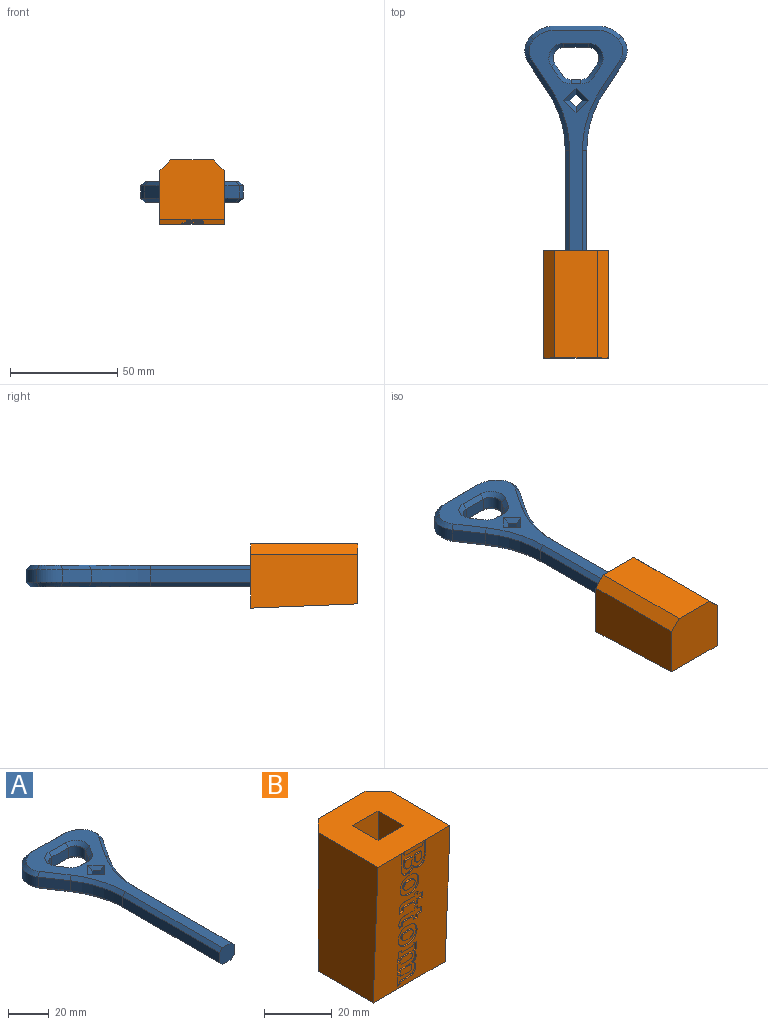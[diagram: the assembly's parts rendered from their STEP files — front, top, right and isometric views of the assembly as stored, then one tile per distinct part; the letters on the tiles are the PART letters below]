
ASSEMBLY  parts=2 mates=1
PART A: 72 faces, bbox 47.8x125x10 mm
  f0: plane 123x43.75mm, normal (0,0,1), area 1271.6mm2, adj f4,f33,f34,f35,f36,f37,f38,f39
  f1: plane 123x43.75mm, normal (0,0,-1), area 1271.6mm2, adj f4,f22,f23,f24,f25,f26,f27,f28
  f2: plane 13.2x8.8mm, normal (-0.83,-0.55,0), area 95.2mm2, adj f19,f20,f24,f35
  f3: plane 66.83x6mm, normal (-1,0,0), area 401mm2, adj f4,f20,f22,f33
  f4: plane 10x10mm, normal (0,-1,0), area 92mm2, adj f0,f1,f3,f5,f22,f32,f33,f43
  f5: plane 66.83x6mm, normal (1,0,0), area 401mm2, adj f4,f21,f32,f43
  f6: plane 13.2x8.8mm, normal (0.83,-0.55,0), area 95.2mm2, adj f18,f21,f30,f41
  f7: plane 20.26x6mm, normal (0,1,0), area 121.6mm2, adj f16,f17,f27,f38
  f8: plane 11.32x6mm, normal (0,-1,0), area 67.9mm2, adj f12,f15,f51,f52
  f9: plane 6x5mm, normal (-0.83,0.55,0), area 36.1mm2, adj f12,f13,f48,f56
  f10: plane 6x4.65mm, normal (0,1,0), area 27.9mm2, adj f13,f14,f44,f59
  f11: plane 6x5mm, normal (0.83,0.55,0), area 36.1mm2, adj f14,f15,f47,f55
  f12: cylinder r=5mm len=7.77mm, axis (0,0,-1), area 64.8mm2, adj f8,f9,f50,f54
  f13: cylinder r=5mm len=6mm, axis (0,0,1), area 29.5mm2, adj f9,f10,f46,f58
  f14: cylinder r=5mm len=6mm, axis (0,0,1), area 29.5mm2, adj f10,f11,f45,f57
  f15: cylinder r=5mm len=7.77mm, axis (0,0,-1), area 64.8mm2, adj f8,f11,f49,f53
  f16: cylinder r=15mm len=11.24mm, axis (0,0,-1), area 76.2mm2, adj f7,f18,f28,f39
  f17: cylinder r=15mm len=11.24mm, axis (0,0,1), area 76.2mm2, adj f7,f19,f26,f37
  f18: cylinder r=10mm len=12.17mm, axis (0,0,-1), area 78.7mm2, adj f6,f16,f29,f40
  f19: cylinder r=10mm len=12.17mm, axis (0,0,1), area 78.7mm2, adj f2,f17,f25,f36
  f20: cylinder r=50mm len=27.74mm, axis (0,0,-1), area 176.4mm2, adj f2,f3,f23,f34
  f21: cylinder r=50mm len=27.74mm, axis (0,0,-1), area 176.4mm2, adj f5,f6,f31,f42
  f22: plane 66.83x2mm, normal (-0.71,0,-0.71), area 189mm2, adj f1,f3,f4,f23
  f23: cone r=52mm half-angle=45deg, axis (0,0,-1), area 84.8mm2, adj f1,f20,f22,f24
  f24: plane 14.31x10.46mm, normal (-0.59,-0.39,-0.71), area 44.9mm2, adj f1,f2,f23,f25
  f25: cone r=8mm half-angle=45deg, axis (0,0,1), area 33.4mm2, adj f1,f19,f24,f26
  f26: cone r=13mm half-angle=45deg, axis (0,0,1), area 33.5mm2, adj f1,f17,f25,f27
  f27: plane 20.26x2mm, normal (0,0.71,-0.71), area 57.3mm2, adj f1,f7,f26,f28
  f28: cone r=13mm half-angle=45deg, axis (0,0,1), area 33.5mm2, adj f1,f16,f27,f29
  f29: cone r=8mm half-angle=45deg, axis (0,0,1), area 33.4mm2, adj f1,f18,f28,f30
  f30: plane 14.31x10.46mm, normal (0.59,-0.39,-0.71), area 44.9mm2, adj f1,f6,f29,f31
  f31: cone r=52mm half-angle=45deg, axis (0,0,-1), area 84.8mm2, adj f1,f21,f30,f32
  f32: plane 66.83x2mm, normal (0.71,0,-0.71), area 189mm2, adj f1,f4,f5,f31
  f33: plane 66.83x2mm, normal (-0.71,0,0.71), area 189mm2, adj f0,f3,f4,f34
  f34: cone r=52mm half-angle=45deg, axis (0,0,1), area 84.8mm2, adj f0,f20,f33,f35
  f35: plane 14.31x10.46mm, normal (-0.59,-0.39,0.71), area 44.9mm2, adj f0,f2,f34,f36
  f36: cone r=8mm half-angle=45deg, axis (0,0,-1), area 33.4mm2, adj f0,f19,f35,f37
  f37: cone r=13mm half-angle=45deg, axis (0,0,-1), area 33.5mm2, adj f0,f17,f36,f38
  f38: plane 20.26x2mm, normal (0,0.71,0.71), area 57.3mm2, adj f0,f7,f37,f39
  f39: cone r=13mm half-angle=45deg, axis (0,0,-1), area 33.5mm2, adj f0,f16,f38,f40
  f40: cone r=8mm half-angle=45deg, axis (0,0,-1), area 33.4mm2, adj f0,f18,f39,f41
  f41: plane 14.31x10.46mm, normal (0.59,-0.39,0.71), area 44.9mm2, adj f0,f6,f40,f42
  f42: cone r=52mm half-angle=45deg, axis (0,0,1), area 84.8mm2, adj f0,f21,f41,f43
  f43: plane 66.83x2mm, normal (0.71,0,0.71), area 189mm2, adj f0,f4,f5,f42
  f44: plane 4.65x2mm, normal (0,0.71,-0.71), area 13.1mm2, adj f1,f10,f45,f46
  f45: cone r=7mm half-angle=45deg, axis (0,0,-1), area 16.7mm2, adj f1,f14,f44,f47
  f46: cone r=7mm half-angle=45deg, axis (0,0,-1), area 16.7mm2, adj f1,f13,f44,f48
  f47: plane 6.11x5mm, normal (0.59,0.39,-0.71), area 17mm2, adj f1,f11,f45,f49
  f48: plane 6.11x5mm, normal (-0.59,0.39,-0.71), area 17mm2, adj f1,f9,f46,f50
  f49: cone r=7mm half-angle=45deg, axis (0,0,-1), area 36.6mm2, adj f1,f15,f47,f51
  f50: cone r=7mm half-angle=45deg, axis (0,0,-1), area 36.6mm2, adj f1,f12,f48,f51
  f51: plane 11.32x2mm, normal (0,-0.71,-0.71), area 32mm2, adj f1,f8,f49,f50
  f52: plane 11.32x2mm, normal (0,-0.71,0.71), area 32mm2, adj f0,f8,f53,f54
  f53: cone r=7mm half-angle=45deg, axis (0,0,1), area 36.6mm2, adj f0,f15,f52,f55
  f54: cone r=7mm half-angle=45deg, axis (0,0,1), area 36.6mm2, adj f0,f12,f52,f56
  f55: plane 6.11x5mm, normal (0.59,0.39,0.71), area 17mm2, adj f0,f11,f53,f57
  f56: plane 6.11x5mm, normal (-0.59,0.39,0.71), area 17mm2, adj f0,f9,f54,f58
  f57: cone r=7mm half-angle=45deg, axis (0,0,1), area 16.7mm2, adj f0,f14,f55,f59
  f58: cone r=7mm half-angle=45deg, axis (0,0,1), area 16.7mm2, adj f0,f13,f56,f59
  f59: plane 4.65x2mm, normal (0,0.71,0.71), area 13.1mm2, adj f0,f10,f57,f58
  f60: plane 6x2.83mm, normal (0.71,0.71,0), area 24mm2, adj f61,f63,f67,f71
  f61: plane 6x2.83mm, normal (-0.71,0.71,0), area 24mm2, adj f60,f62,f65,f69
  f62: plane 6x2.83mm, normal (-0.71,-0.71,0), area 24mm2, adj f61,f63,f64,f68
  f63: plane 6x2.83mm, normal (0.71,-0.71,0), area 24mm2, adj f60,f62,f66,f70
  f64: plane 5.66x5.66mm, normal (-0.5,-0.5,-0.71), area 17mm2, adj f1,f62,f65,f66
  f65: plane 5.66x5.66mm, normal (-0.5,0.5,-0.71), area 17mm2, adj f1,f61,f64,f67
  f66: plane 5.66x5.66mm, normal (0.5,-0.5,-0.71), area 17mm2, adj f1,f63,f64,f67
  f67: plane 5.66x5.66mm, normal (0.5,0.5,-0.71), area 17mm2, adj f1,f60,f65,f66
  f68: plane 5.66x5.66mm, normal (-0.5,-0.5,0.71), area 17mm2, adj f0,f62,f69,f70
  f69: plane 5.66x5.66mm, normal (-0.5,0.5,0.71), area 17mm2, adj f0,f61,f68,f71
  f70: plane 5.66x5.66mm, normal (0.5,-0.5,0.71), area 17mm2, adj f0,f63,f68,f71
  f71: plane 5.66x5.66mm, normal (0.5,0.5,0.71), area 17mm2, adj f0,f60,f69,f70
PART B: 175 faces, bbox 30x30x50 mm
  f0: plane 50x30mm, normal (0,-1,-0.04), area 1230.9mm2, adj f2,f7,f8,f10,f11,f12,f13,f14
  f1: plane 50x20mm, normal (0,1,0), area 1000mm2, adj f8,f10,f173,f174
  f2: plane 50x25mm, normal (-1,0,0), area 1200mm2, adj f0,f8,f10,f173
  f3: plane 20x10.5mm, normal (1,0,0), area 210mm2, adj f4,f6,f8,f9
  f4: plane 20x10.5mm, normal (0,-1,0), area 210mm2, adj f3,f5,f8,f9
  f5: plane 20x10.5mm, normal (-1,0,0), area 210mm2, adj f4,f6,f8,f9
  f6: plane 20x10.5mm, normal (0,1,0), area 210mm2, adj f3,f5,f8,f9
  f7: plane 50x25mm, normal (1,0,0), area 1200mm2, adj f0,f8,f10,f174
  f8: plane 30x30mm, normal (0,0,1), area 764.7mm2, adj f0,f1,f2,f3,f4,f5,f6,f7
  f9: plane 10.5x10.5mm, normal (0,0,1), area 110.3mm2, adj f3,f4,f5,f6
  f10: plane 30x28mm, normal (0,0,-1), area 815mm2, adj f0,f1,f2,f7,f173,f174
  f11: plane 2.04x0.58mm, normal (-1,0,0), area 1mm2, adj f0,f12,f30,f31
  f12: plane 1.84x0.5mm, normal (0,0.04,-1), area 0.9mm2, adj f0,f11,f13,f31
  f13: plane 1.12x0.54mm, normal (-1,0,0), area 0.6mm2, adj f0,f12,f14,f31
  f14: plane 1.42x0.5mm, normal (0,0.04,-1), area 0.7mm2, adj f0,f13,f15,f31
  f15: plane 1.12x0.54mm, normal (1,0,0), area 0.6mm2, adj f0,f14,f16,f31
  f16: plane 3.84x0.5mm, normal (0,0.04,-1), area 1.9mm2, adj f0,f15,f17,f31
  f17: extruded ~1.83x0.59mm, area 1mm2, adj f0,f16,f18,f31
  f18: extruded ~1.64x0.58mm, area 0.9mm2, adj f0,f17,f19,f31
  f19: extruded ~0.74x0.53mm, area 0.4mm2, adj f0,f18,f20,f31
  f20: extruded ~0.69x0.53mm, area 0.3mm2, adj f0,f19,f21,f31
  f21: plane 1.47x0.51mm, normal (-0.12,-0.04,0.99), area 0.7mm2, adj f0,f20,f22,f31
  f22: extruded ~0.51x0.37mm, area 0.2mm2, adj f0,f21,f23,f31
  f23: extruded ~0.51x0.38mm, area 0.2mm2, adj f0,f22,f24,f31
  f24: extruded ~0.52x0.51mm, area 0.3mm2, adj f0,f23,f25,f31
  f25: extruded ~0.63x0.51mm, area 0.3mm2, adj f0,f24,f26,f31
  f26: plane 3.83x0.5mm, normal (0,-0.04,1), area 1.9mm2, adj f0,f25,f27,f31
  f27: plane 1.34x0.55mm, normal (1,0,0), area 0.7mm2, adj f0,f26,f28,f31
  f28: plane 1.42x0.5mm, normal (0,-0.04,1), area 0.7mm2, adj f0,f27,f29,f31
  f29: plane 1.34x0.55mm, normal (-1,0,0), area 0.7mm2, adj f0,f28,f30,f31
  f30: plane 1.84x0.5mm, normal (0,-0.04,1), area 0.9mm2, adj f0,f11,f29,f31
  f31: plane 9.51x4.68mm, normal (0,-1,-0.04), area 24.2mm2, adj f11,f12,f13,f14,f15,f16,f17,f18
  f32: plane 0.5x0.15mm, normal (0,0.04,-1), area 0.1mm2, adj f0,f33,f51,f52
  f33: extruded ~2.76x0.96mm, area 1.5mm2, adj f0,f32,f34,f52
  f34: extruded ~2.63x1.07mm, area 1.5mm2, adj f0,f33,f35,f52
  f35: extruded ~2.61x1.07mm, area 1.4mm2, adj f0,f34,f36,f52
  f36: extruded ~2.76x0.96mm, area 1.5mm2, adj f0,f35,f37,f52
  f37: plane 0.5x0.15mm, normal (0,-0.04,1), area 0.1mm2, adj f0,f36,f38,f52
  f38: extruded ~2.76x0.96mm, area 1.5mm2, adj f0,f37,f39,f52
  f39: extruded ~2.63x1.07mm, area 1.5mm2, adj f0,f38,f40,f52
  f40: extruded ~2.62x1.07mm, area 1.5mm2, adj f0,f39,f51,f52
  f41: plane 0.5x0.15mm, normal (0,-0.04,1), area 0.1mm2, adj f42,f50,f52,f53
  f42: extruded ~1.63x0.51mm, area 0.8mm2, adj f41,f43,f52,f53
  f43: extruded ~1.17x0.63mm, area 0.7mm2, adj f42,f44,f52,f53
  f44: extruded ~1.18x0.63mm, area 0.7mm2, adj f43,f45,f52,f53
  f45: extruded ~1.63x0.51mm, area 0.8mm2, adj f44,f46,f52,f53
  f46: plane 0.5x0.15mm, normal (0,0.04,-1), area 0.1mm2, adj f45,f47,f52,f53
  f47: extruded ~1.65x0.51mm, area 0.9mm2, adj f46,f48,f52,f53
  f48: extruded ~1.17x0.63mm, area 0.7mm2, adj f47,f49,f52,f53
  f49: extruded ~1.19x0.62mm, area 0.7mm2, adj f48,f50,f52,f53
  f50: extruded ~1.65x0.51mm, area 0.9mm2, adj f41,f49,f52,f53
  f51: extruded ~2.76x0.96mm, area 1.5mm2, adj f0,f32,f40,f52
  f52: plane 7.8x7.09mm, normal (0,-1,-0.04), area 33.2mm2, adj f32,f33,f34,f35,f36,f37,f38,f39
  f53: plane 4.69x3.04mm, normal (0,-1,-0.04), area 11.9mm2, adj f41,f42,f43,f44,f45,f46,f47,f48
  f54: plane 0.5x0.15mm, normal (0,0.04,-1), area 0.1mm2, adj f0,f55,f73,f74
  f55: extruded ~2.76x0.96mm, area 1.5mm2, adj f0,f54,f56,f74
  f56: extruded ~2.63x1.07mm, area 1.5mm2, adj f0,f55,f57,f74
  f57: extruded ~2.61x1.07mm, area 1.4mm2, adj f0,f56,f58,f74
  f58: extruded ~2.76x0.96mm, area 1.5mm2, adj f0,f57,f59,f74
  f59: plane 0.5x0.15mm, normal (0,-0.04,1), area 0.1mm2, adj f0,f58,f60,f74
  f60: extruded ~2.76x0.96mm, area 1.5mm2, adj f0,f59,f61,f74
  f61: extruded ~2.63x1.07mm, area 1.5mm2, adj f0,f60,f62,f74
  f62: extruded ~2.62x1.07mm, area 1.5mm2, adj f0,f61,f73,f74
  f63: plane 0.5x0.15mm, normal (0,-0.04,1), area 0.1mm2, adj f64,f72,f74,f75
  f64: extruded ~1.63x0.51mm, area 0.8mm2, adj f63,f65,f74,f75
  f65: extruded ~1.17x0.63mm, area 0.7mm2, adj f64,f66,f74,f75
  f66: extruded ~1.18x0.63mm, area 0.7mm2, adj f65,f67,f74,f75
  f67: extruded ~1.63x0.51mm, area 0.8mm2, adj f66,f68,f74,f75
  f68: plane 0.5x0.15mm, normal (0,0.04,-1), area 0.1mm2, adj f67,f69,f74,f75
  f69: extruded ~1.65x0.51mm, area 0.9mm2, adj f68,f70,f74,f75
  f70: extruded ~1.17x0.63mm, area 0.7mm2, adj f69,f71,f74,f75
  f71: extruded ~1.19x0.62mm, area 0.7mm2, adj f70,f72,f74,f75
  f72: extruded ~1.65x0.51mm, area 0.9mm2, adj f63,f71,f74,f75
  f73: extruded ~2.76x0.96mm, area 1.5mm2, adj f0,f54,f62,f74
  f74: plane 7.8x7.09mm, normal (0,-1,-0.04), area 33.2mm2, adj f54,f55,f56,f57,f58,f59,f60,f61
  f75: plane 4.69x3.04mm, normal (0,-1,-0.04), area 11.9mm2, adj f63,f64,f65,f66,f67,f68,f69,f70
  f76: plane 1.1x0.54mm, normal (0.98,0.01,-0.19), area 0.6mm2, adj f0,f77,f118,f119
  f77: plane 4.66x0.5mm, normal (0,0.04,-1), area 2.3mm2, adj f0,f76,f78,f119
  f78: plane 1x0.54mm, normal (-0.98,0.01,-0.21), area 0.5mm2, adj f0,f77,f79,f119
  f79: plane 1.22x0.5mm, normal (0,0.04,-1), area 0.6mm2, adj f0,f78,f80,f119
  f80: plane 3.89x0.65mm, normal (1,0,0), area 1.9mm2, adj f0,f79,f81,f119
  f81: plane 1.22x0.5mm, normal (0,-0.04,1), area 0.6mm2, adj f0,f80,f82,f119
  f82: plane 0.89x0.53mm, normal (-0.97,-0.01,0.23), area 0.4mm2, adj f0,f81,f83,f119
  f83: plane 4.06x0.5mm, normal (0,-0.04,1), area 2mm2, adj f0,f82,f84,f119
  f84: extruded ~0.53x0.52mm, area 0.3mm2, adj f0,f83,f85,f119
  f85: extruded ~0.74x0.53mm, area 0.4mm2, adj f0,f84,f86,f119
  f86: extruded ~0.85x0.53mm, area 0.5mm2, adj f0,f85,f87,f119
  f87: extruded ~1.18x0.51mm, area 0.6mm2, adj f0,f86,f88,f119
  f88: plane 3.13x0.5mm, normal (0,0.04,-1), area 1.6mm2, adj f0,f87,f89,f119
  f89: plane 0.84x0.53mm, normal (-0.97,0.01,-0.25), area 0.4mm2, adj f0,f88,f90,f119
  f90: plane 1.22x0.5mm, normal (0,0.04,-1), area 0.6mm2, adj f0,f89,f91,f119
  f91: plane 3.68x0.65mm, normal (1,0,0), area 1.8mm2, adj f0,f90,f92,f119
  f92: plane 1.22x0.5mm, normal (0,-0.04,1), area 0.6mm2, adj f0,f91,f93,f119
  f93: plane 0.84x0.53mm, normal (-0.97,-0.01,0.25), area 0.4mm2, adj f0,f92,f94,f119
  f94: plane 3.52x0.5mm, normal (0,-0.04,1), area 1.8mm2, adj f0,f93,f95,f119
  f95: extruded ~0.5x0.19mm, area 0.1mm2, adj f0,f94,f96,f119
  f96: extruded ~0.5x0.22mm, area 0.1mm2, adj f0,f95,f97,f119
  f97: extruded ~0.53x0.52mm, area 0.4mm2, adj f0,f96,f98,f119
  f98: extruded ~0.77x0.53mm, area 0.4mm2, adj f0,f97,f99,f119
  f99: extruded ~0.85x0.53mm, area 0.5mm2, adj f0,f98,f100,f119
  f100: extruded ~1.19x0.51mm, area 0.6mm2, adj f0,f99,f101,f119
  f101: plane 3.13x0.5mm, normal (0,0.04,-1), area 1.6mm2, adj f0,f100,f102,f119
  f102: plane 0.9x0.53mm, normal (-0.97,0.01,-0.23), area 0.5mm2, adj f0,f101,f103,f119
  f103: plane 1.22x0.5mm, normal (0,0.04,-1), area 0.6mm2, adj f0,f102,f104,f119
  f104: plane 3.9x0.66mm, normal (1,0,0), area 1.9mm2, adj f0,f103,f105,f119
  f105: plane 1.22x0.5mm, normal (0,-0.04,1), area 0.6mm2, adj f0,f104,f106,f119
  f106: plane 1x0.54mm, normal (-0.98,-0.01,0.21), area 0.5mm2, adj f0,f105,f107,f119
  f107: plane 3.13x0.5mm, normal (0,-0.04,1), area 1.6mm2, adj f0,f106,f108,f119
  f108: extruded ~2.34x0.66mm, area 1.2mm2, adj f0,f107,f109,f119
  f109: extruded ~1.77x0.77mm, area 1mm2, adj f0,f108,f110,f119
  f110: extruded ~1.33x0.55mm, area 0.7mm2, adj f0,f109,f111,f119
  f111: extruded ~0.95x0.92mm, area 0.7mm2, adj f0,f110,f112,f119
  f112: extruded ~0.97x0.8mm, area 0.6mm2, adj f0,f111,f113,f119
  f113: extruded ~1.26x0.55mm, area 0.6mm2, adj f0,f112,f114,f119
  f114: extruded ~1.28x0.55mm, area 0.7mm2, adj f0,f113,f115,f119
  f115: extruded ~0.93x0.84mm, area 0.6mm2, adj f0,f114,f116,f119
  f116: plane 0.99x0.5mm, normal (-0.08,-0.04,1), area 0.5mm2, adj f0,f115,f117,f119
  f117: plane 2.98x0.62mm, normal (-1,0,0), area 1.5mm2, adj f0,f116,f118,f119
  f118: plane 1.22x0.5mm, normal (0,0.04,-1), area 0.6mm2, adj f0,f76,f117,f119
  f119: plane 12.81x7.66mm, normal (0,-1,-0.04), area 59.6mm2, adj f76,f77,f78,f79,f80,f81,f82,f83
  f120: plane 2.04x0.58mm, normal (-1,0,0), area 1mm2, adj f0,f121,f139,f140
  f121: plane 1.84x0.5mm, normal (0,0.04,-1), area 0.9mm2, adj f0,f120,f122,f140
  f122: plane 1.12x0.54mm, normal (-1,0,0), area 0.6mm2, adj f0,f121,f123,f140
  f123: plane 1.42x0.5mm, normal (0,0.04,-1), area 0.7mm2, adj f0,f122,f124,f140
  f124: plane 1.12x0.54mm, normal (1,0,0), area 0.6mm2, adj f0,f123,f125,f140
  f125: plane 3.84x0.5mm, normal (0,0.04,-1), area 1.9mm2, adj f0,f124,f126,f140
  f126: extruded ~1.83x0.59mm, area 1mm2, adj f0,f125,f127,f140
  f127: extruded ~1.64x0.58mm, area 0.9mm2, adj f0,f126,f128,f140
  f128: extruded ~0.74x0.53mm, area 0.4mm2, adj f0,f127,f129,f140
  f129: extruded ~0.69x0.53mm, area 0.3mm2, adj f0,f128,f130,f140
  f130: plane 1.47x0.51mm, normal (-0.12,-0.04,0.99), area 0.7mm2, adj f0,f129,f131,f140
  f131: extruded ~0.51x0.37mm, area 0.2mm2, adj f0,f130,f132,f140
  f132: extruded ~0.51x0.38mm, area 0.2mm2, adj f0,f131,f133,f140
  f133: extruded ~0.52x0.51mm, area 0.3mm2, adj f0,f132,f134,f140
  f134: extruded ~0.63x0.51mm, area 0.3mm2, adj f0,f133,f135,f140
  f135: plane 3.83x0.5mm, normal (0,-0.04,1), area 1.9mm2, adj f0,f134,f136,f140
  f136: plane 1.34x0.55mm, normal (1,0,0), area 0.7mm2, adj f0,f135,f137,f140
  f137: plane 1.42x0.5mm, normal (0,-0.04,1), area 0.7mm2, adj f0,f136,f138,f140
  f138: plane 1.34x0.55mm, normal (-1,0,0), area 0.7mm2, adj f0,f137,f139,f140
  f139: plane 1.84x0.5mm, normal (0,-0.04,1), area 0.9mm2, adj f0,f120,f138,f140
  f140: plane 9.51x4.68mm, normal (0,-1,-0.04), area 24.2mm2, adj f120,f121,f122,f123,f124,f125,f126,f127
  f141: plane 4.51x0.68mm, normal (-1,0,0), area 2.2mm2, adj f0,f142,f169,f170
  f142: plane 1.22x0.5mm, normal (0,0.04,-1), area 0.6mm2, adj f0,f141,f143,f170
  f143: plane 1.1x0.54mm, normal (0.98,0.01,-0.19), area 0.5mm2, adj f0,f142,f144,f170
  f144: plane 7.26x0.5mm, normal (0,0.04,-1), area 3.6mm2, adj f0,f143,f145,f170
  f145: plane 1.1x0.54mm, normal (-0.98,0.01,-0.19), area 0.5mm2, adj f0,f144,f146,f170
  f146: plane 1.22x0.5mm, normal (0,0.04,-1), area 0.6mm2, adj f0,f145,f147,f170
  f147: plane 4.99x0.7mm, normal (1,0,0), area 2.5mm2, adj f0,f146,f148,f170
  f148: extruded ~2.73x0.75mm, area 1.4mm2, adj f0,f147,f149,f170
  f149: extruded ~2.2x0.98mm, area 1.2mm2, adj f0,f148,f150,f170
  f150: extruded ~1.48x0.52mm, area 0.8mm2, adj f0,f149,f151,f170
  f151: extruded ~1.38x0.84mm, area 0.8mm2, adj f0,f150,f152,f170
  f152: extruded ~1.1x0.83mm, area 0.7mm2, adj f0,f151,f153,f170
  f153: extruded ~1.25x0.51mm, area 0.7mm2, adj f0,f152,f154,f170
  f154: extruded ~2.08x1.02mm, area 1.2mm2, adj f0,f153,f169,f170
  f155: plane 2.04x0.58mm, normal (1,0,0), area 1mm2, adj f156,f167,f170,f172
  f156: extruded ~1.16x0.55mm, area 0.6mm2, adj f155,f157,f170,f172
  f157: extruded ~1.14x0.51mm, area 0.6mm2, adj f156,f158,f170,f172
  f158: extruded ~1.04x0.52mm, area 0.6mm2, adj f157,f159,f170,f172
  f159: extruded ~1.25x0.55mm, area 0.7mm2, adj f158,f160,f170,f172
  f160: plane 1.89x0.57mm, normal (-1,0,0), area 0.9mm2, adj f159,f167,f170,f172
  f161: plane 2.68x0.5mm, normal (0,-0.04,1), area 1.3mm2, adj f162,f168,f170,f171
  f162: plane 1.41x0.56mm, normal (1,0,0), area 0.7mm2, adj f161,f163,f170,f171
  f163: extruded ~1.34x0.55mm, area 0.7mm2, adj f162,f164,f170,f171
  f164: extruded ~1.04x0.52mm, area 0.6mm2, adj f163,f165,f170,f171
  f165: extruded ~0.97x0.52mm, area 0.6mm2, adj f164,f166,f170,f171
  f166: extruded ~1.27x0.55mm, area 0.7mm2, adj f165,f168,f170,f171
  f167: plane 2.92x0.5mm, normal (0,-0.04,1), area 1.5mm2, adj f155,f160,f170,f172
  f168: plane 1.48x0.56mm, normal (-1,0,0), area 0.7mm2, adj f161,f166,f170,f171
  f169: extruded ~2.8x0.7mm, area 1.5mm2, adj f0,f141,f154,f170
  f170: plane 10.12x8.65mm, normal (0,-1,-0.04), area 55mm2, adj f141,f142,f143,f144,f145,f146,f147,f148
  f171: plane 3.15x2.68mm, normal (0,-1,-0.04), area 7.6mm2, adj f161,f162,f163,f164,f165,f166,f168
  f172: plane 3.52x2.92mm, normal (0,-1,-0.04), area 9.5mm2, adj f155,f156,f157,f158,f159,f160,f167
  f173: plane 50x5mm, normal (-0.71,0.71,0), area 353.6mm2, adj f1,f2,f8,f10
  f174: plane 50x5mm, normal (0.71,0.71,0), area 353.6mm2, adj f1,f7,f8,f10
PLACE A t=(0,50,-5)mm
PLACE B rot(axis=(0,0.71,0.71),180deg) t=(0,0,0)mm
MATE fastened B.f9 <-> A.f4  axis (0,1,0) through (0,0,0)mm
